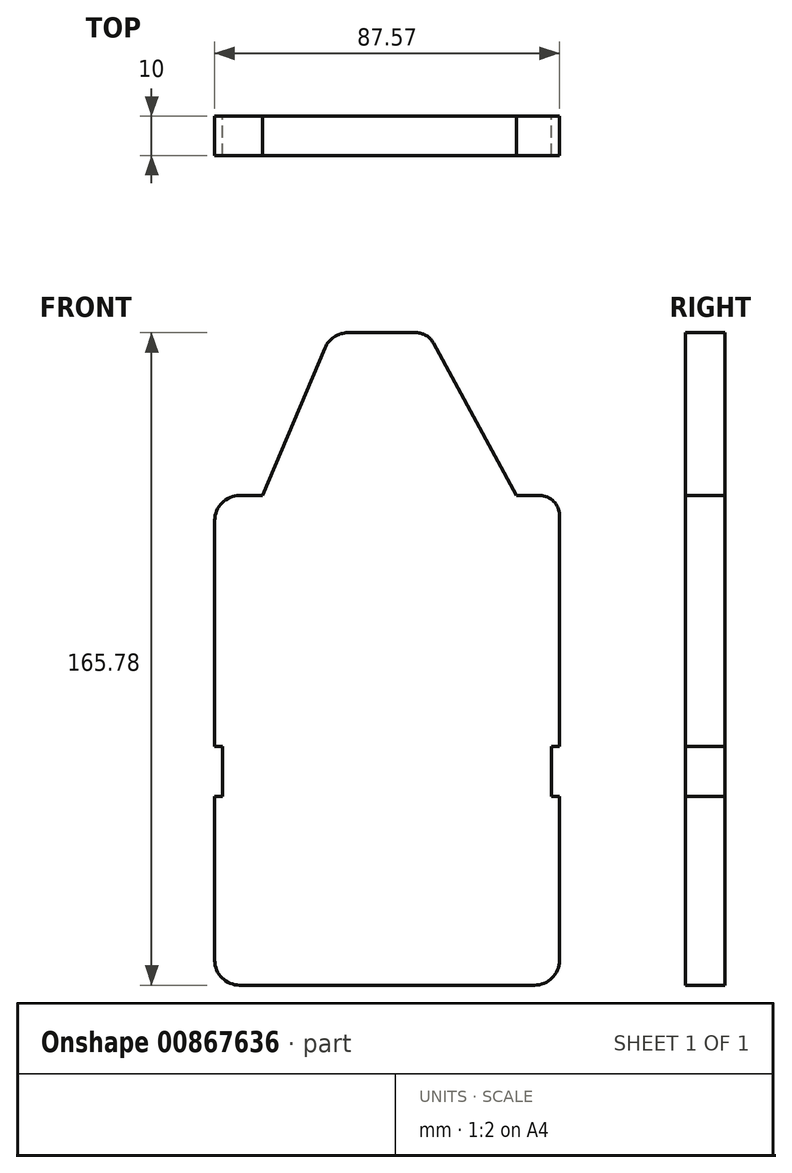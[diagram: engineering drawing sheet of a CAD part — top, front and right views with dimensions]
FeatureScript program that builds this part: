
annotation { "Feature Type Name" : "Feature", "Feature Type Description" : "" }
export const myFeature = defineFeature(function(context is Context, id is Id, definition is map)
    precondition{}
    {
        {
            var Q0;
            Q0=qCreatedBy(makeId("Front.planeOp"),FACE);
            var sketch = newSketch(context, id + "F0", { "sketchPlane" : qUnion([Q0])});
            skLineSegment(sketch, "E0", {"start": v(0, 105.13) * mm, "end": v(-10.79, 105.13) * mm});
            skLineSegment(sketch, "E1", {"start": v(-16.64, 101.26) * mm, "end": v(-32.48, 63.77) * mm});
            skLineSegment(sketch, "E2", {"start": v(-32.48, 63.77) * mm, "end": v(-38.3, 63.77) * mm});
            skLineSegment(sketch, "E3", {"start": v(-44.66, 57.42) * mm, "end": v(-44.66, 0) * mm});
            skLineSegment(sketch, "E4", {"start": v(-44.66, 0) * mm, "end": v(-42.66, 0) * mm});
            skLineSegment(sketch, "E5", {"start": v(-42.66, 0) * mm, "end": v(-42.66, -12.67) * mm});
            skLineSegment(sketch, "E6", {"start": v(-42.66, -12.67) * mm, "end": v(-44.66, -12.67) * mm});
            skLineSegment(sketch, "E7", {"start": v(-44.66, -12.67) * mm, "end": v(-44.66, -54.3) * mm});
            skLineSegment(sketch, "E8", {"start": v(-38.3, -60.65) * mm, "end": v(0, -60.65) * mm});
            skLineSegment(sketch, "E9", {"start": v(0, -60.65) * mm, "end": v(36.56, -60.65) * mm});
            skLineSegment(sketch, "E10", {"start": v(42.91, -54.3) * mm, "end": v(42.91, -12.67) * mm});
            skLineSegment(sketch, "E11", {"start": v(42.91, -12.67) * mm, "end": v(40.91, -12.67) * mm});
            skLineSegment(sketch, "E12", {"start": v(40.91, -12.67) * mm, "end": v(40.91, 0) * mm});
            skLineSegment(sketch, "E13", {"start": v(40.91, 0) * mm, "end": v(42.91, 0) * mm});
            skLineSegment(sketch, "E14", {"start": v(42.91, 0) * mm, "end": v(42.91, 58.77) * mm});
            skLineSegment(sketch, "E15", {"start": v(37.91, 63.77) * mm, "end": v(32, 63.77) * mm});
            skLineSegment(sketch, "E16", {"start": v(32, 63.77) * mm, "end": v(10.9, 102.53) * mm});
            skLineSegment(sketch, "E17", {"start": v(0, 105.13) * mm, "end": v(6.51, 105.13) * mm});
            skPoint(sketch, "E18.visualSharp", {"position": v(-44.66, 63.77) * mm});
            skArc(sketch, "E18.filletArc", {"start": v(-38.3, 63.77) * mm, "mid": v(-42.8, 61.9) * mm, "end": v(-44.66, 57.42) * mm});
            skPoint(sketch, "E19.visualSharp", {"position": v(42.91, 63.77) * mm});
            skArc(sketch, "E19.filletArc", {"start": v(42.91, 58.77) * mm, "mid": v(41.45, 62.3) * mm, "end": v(37.91, 63.77) * mm});
            skPoint(sketch, "E20.visualSharp", {"position": v(9.48, 105.13) * mm});
            skArc(sketch, "E20.filletArc", {"start": v(10.9, 102.53) * mm, "mid": v(9.07, 104.43) * mm, "end": v(6.51, 105.13) * mm});
            skPoint(sketch, "E21.visualSharp", {"position": v(-15, 105.13) * mm});
            skArc(sketch, "E21.filletArc", {"start": v(-10.79, 105.13) * mm, "mid": v(-14.3, 104.08) * mm, "end": v(-16.64, 101.26) * mm});
            skPoint(sketch, "E22.visualSharp", {"position": v(42.91, -60.65) * mm});
            skArc(sketch, "E22.filletArc", {"start": v(36.56, -60.65) * mm, "mid": v(41.05, -58.79) * mm, "end": v(42.91, -54.3) * mm});
            skPoint(sketch, "E23.visualSharp", {"position": v(-44.66, -60.65) * mm});
            skArc(sketch, "E23.filletArc", {"start": v(-44.66, -54.3) * mm, "mid": v(-42.8, -58.79) * mm, "end": v(-38.3, -60.65) * mm});
            skSolve(sketch);
        }
        {
            var Q0;
            Q0=makeQuery(id+"F0.imprint","IMPRINT",FACE,{"disambiguationData":[TD([[makeQuery(id+"F0.imprint","IMPRINT",EDGE,{"derivedFrom":sQuery(id+"F0.wireOp",EDGE,"E0")}),1.0]])]});
            extrude(context, id + "F1", {"entities" : qUnion([Q0]), "depth" : 10 * mm, "offsetDistance" : 25.4 * mm});
        }
    });
